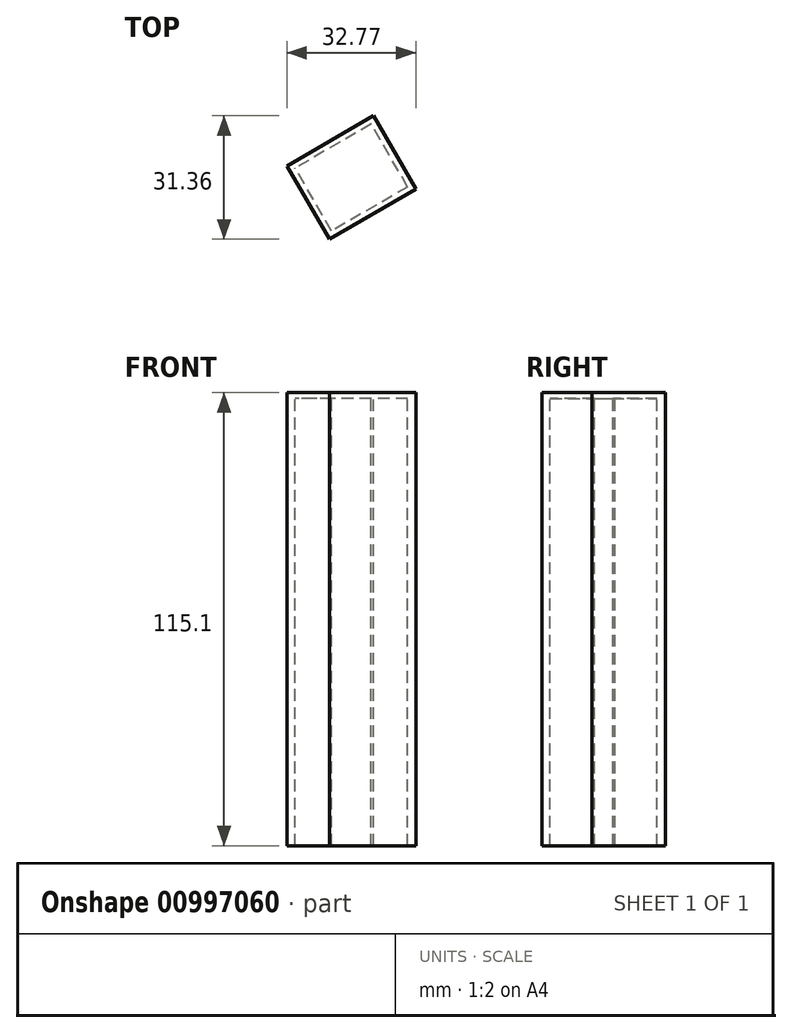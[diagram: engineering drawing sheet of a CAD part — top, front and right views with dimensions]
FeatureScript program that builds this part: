
annotation { "Feature Type Name" : "Feature", "Feature Type Description" : "" }
export const myFeature = defineFeature(function(context is Context, id is Id, definition is map)
    precondition{}
    {
        {
            var Q0;
            Q0=qCreatedBy(makeId("Top.planeOp"),FACE);
            var sketch = newSketch(context, id + "F0", { "sketchPlane" : qUnion([Q0])});
            skLineSegment(sketch, "E0", {"start": v(-45.16, 44.48) * mm, "end": v(0, -41.62) * mm});
            skLineSegment(sketch, "E1", {"start": v(0, -41.62) * mm, "end": v(0, 54.68) * mm});
            skLineSegment(sketch, "E2", {"start": v(0, 54.68) * mm, "end": v(-10.8, 73.28) * mm});
            skSolve(sketch);
        }
        {
            var Q0;
            Q0=sQuery(id+"F0.wireOp",EDGE,"E1");
            var Q1;
            Q1=sQuery(id+"F0.wireOp",EDGE,"E0");
            var Q2;
            Q2=sQuery(id+"F0.wireOp",EDGE,"E2");
            extrude(context, id + "F1", {"bodyType" : ToolBodyType.SURFACE, "surfaceEntities" : qUnion([Q0, Q1, Q2]), "depth" : 115.1 * mm, "offsetDistance" : 25.4 * mm});
        }
        {
            var Q0;
            Q0=makeQuery(id+"F1.opExtrude","SWEPT_FACE",FACE,{"disambiguationData":[OSD([sQuery(id+"F0.wireOp",EDGE,"E0")])]});
            var sketch = newSketch(context, id + "F2", { "sketchPlane" : qUnion([Q0])});
            skSolve(sketch);
        }
        {
            var Q0;
            Q0=makeQuery(id+"F1.opExtrude","SWEPT_FACE",FACE,{"disambiguationData":[OSD([sQuery(id+"F0.wireOp",EDGE,"E2")])]});
            extrude(context, id + "F3", {"entities" : qUnion([Q0]), "depth" : 25.4 * mm, "offsetDistance" : 25.4 * mm});
        }
        {
            var Q0;
            {var subQ0=sQuery(id+"F0.wireOp",EDGE,"E2");Q0=makeQuery(id+"F3.opExtrude","SWEPT_FACE",FACE,{"disambiguationData":[OSD([subQ0]),TDD([makeQuery(id+"F1.opExtrude","CAP_EDGE",EDGE,{"disambiguationData":[OSD([subQ0])],"isStart":true})])]});}
            shell(context, id + "F4", {"entities" : qUnion([Q0]), "thickness" : 1.52 * mm});
        }
    });
